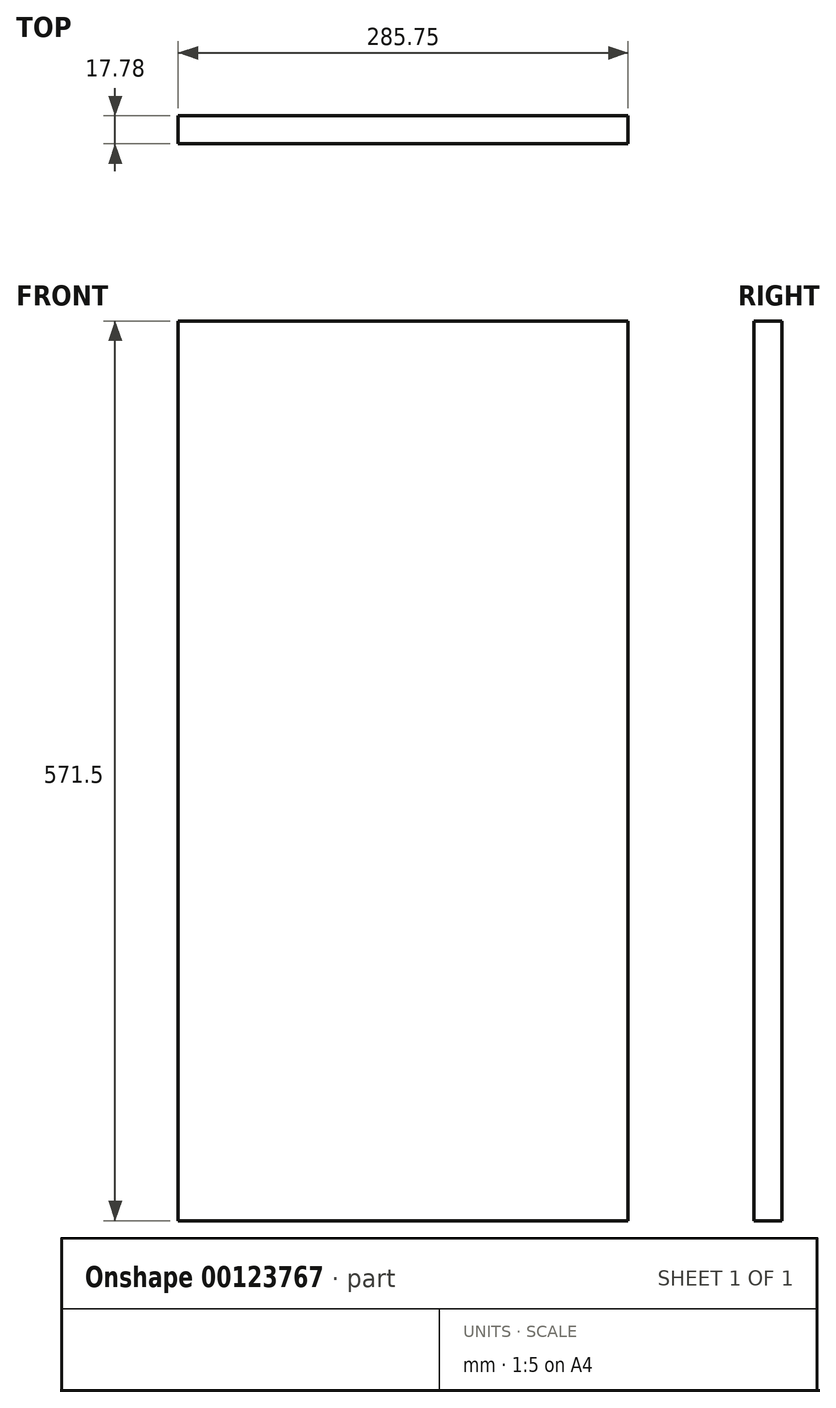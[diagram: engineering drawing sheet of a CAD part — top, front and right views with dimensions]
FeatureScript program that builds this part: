
annotation { "Feature Type Name" : "Feature", "Feature Type Description" : "" }
export const myFeature = defineFeature(function(context is Context, id is Id, definition is map)
    precondition{}
    {
        {
            var Q0;
            Q0=qCreatedBy(makeId("Front.planeOp"),FACE);
            var sketch = newSketch(context, id + "F0", { "sketchPlane" : qUnion([Q0])});
            skLineSegment(sketch, "E0.bottom", {"start": v(-183.93, 373.35) * mm, "end": v(101.82, 373.35) * mm});
            skLineSegment(sketch, "E0.top", {"start": v(-183.93, -198.15) * mm, "end": v(101.82, -198.15) * mm});
            skLineSegment(sketch, "E0.left", {"start": v(-183.93, 373.35) * mm, "end": v(-183.93, -198.15) * mm});
            skLineSegment(sketch, "E0.right", {"start": v(101.82, 373.35) * mm, "end": v(101.82, -198.15) * mm});
            skSolve(sketch);
        }
        {
            var Q0;
            Q0=makeQuery(id+"F0.imprint","IMPRINT",FACE,{"disambiguationData":[TD([[makeQuery(id+"F0.imprint","IMPRINT",EDGE,{"derivedFrom":sQuery(id+"F0.wireOp",EDGE,"E0.bottom")}),-1.0]])]});
            extrude(context, id + "F1", {"entities" : qUnion([Q0]), "depth" : 17.78 * mm});
        }
    });
